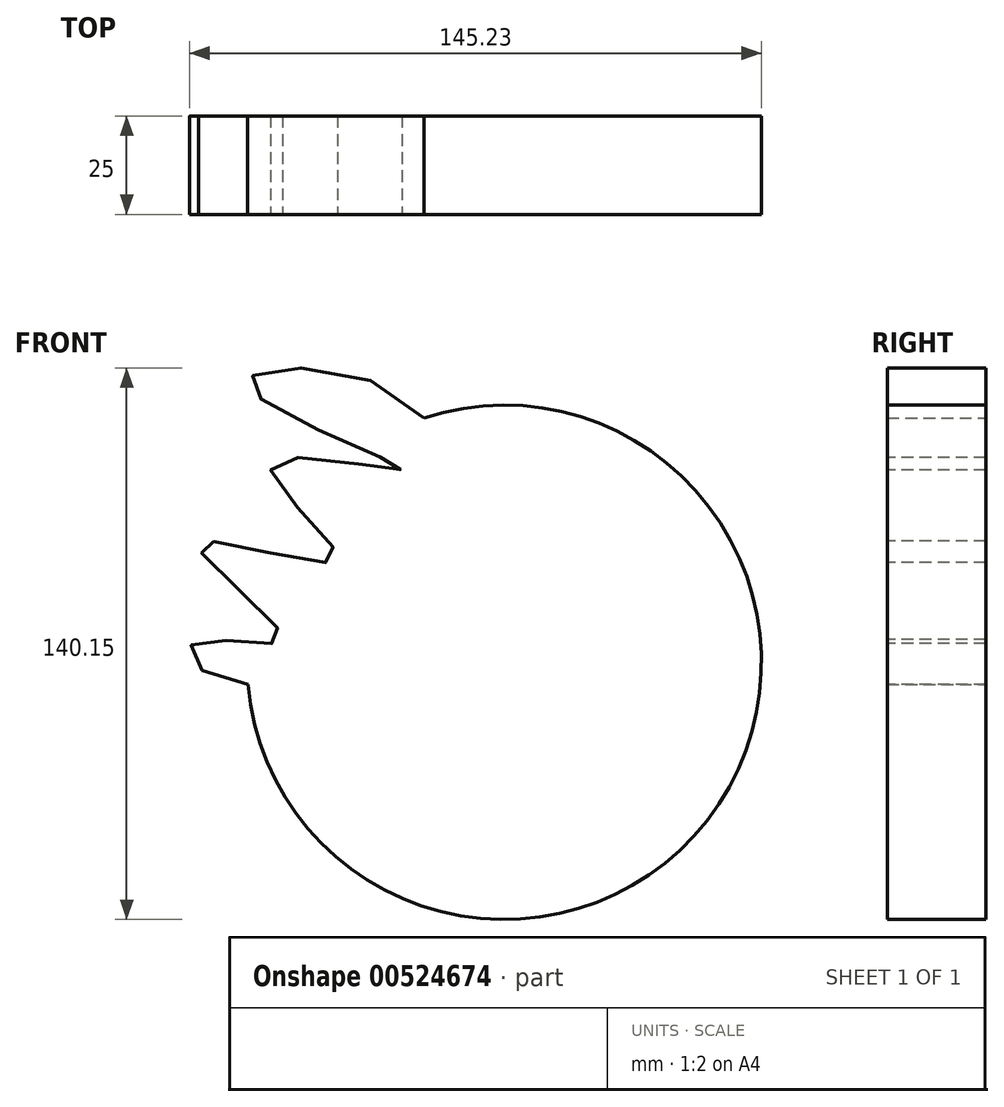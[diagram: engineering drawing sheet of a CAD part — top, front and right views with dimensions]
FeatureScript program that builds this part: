
annotation { "Feature Type Name" : "Feature", "Feature Type Description" : "" }
export const myFeature = defineFeature(function(context is Context, id is Id, definition is map)
    precondition{}
    {
        {
            var Q0;
            Q0=qCreatedBy(makeId("Front.planeOp"),FACE);
            var sketch = newSketch(context, id + "F0", { "sketchPlane" : qUnion([Q0])});
            skArc(sketch, "E0", {"start": v(-74.78, 0) * mm, "mid": v(44.84, -30.44) * mm, "end": v(-30.03, 67.7) * mm});
            skFitSpline(sketch, "E1", {"points": [v(-74.78, 0) * mm, v(-88.66, 10.48) * mm, v(-66, 11.61) * mm, v(-87.25, 35.7) * mm, v(-52.12, 31.73) * mm, v(-68.84, 55.8) * mm, v(-35.7, 54.67) * mm, v(-74.78, 76.2) * mm, v(-30.03, 67.7) * mm, v(-74.78, 0) * mm]});
            skSolve(sketch);
        }
        {
            var Q0;
            {var subQ0=sQuery(id+"F0.wireOp",EDGE,"E0");Q0=makeQuery(id+"F0.imprint","IMPRINT",FACE,{"disambiguationData":[TD([[makeQuery(id+"F0.imprint","IMPRINT",EDGE,{"derivedFrom":subQ0}),1.0]])]});}
            var Q1;
            {var subQ0=sQuery(id+"F0.wireOp",EDGE,"E1");var subQ1=sQuery(id+"F0.wireOp",EDGE,"E0");var subQ2=makeQuery(id+"F0.imprint","INTERSECT",VERTEX,{"disambiguationData":[OD(0.0)],"derivedFrom":[subQ1,subQ0]});Q1=makeQuery(id+"F0.imprint","IMPRINT",FACE,{"disambiguationData":[TD([[makeQuery(id+"F0.imprint","IMPRINT",EDGE,{"disambiguationData":[TD([[subQ2,-1.0]])],"derivedFrom":subQ0}),-1.0]])]});}
            extrude(context, id + "F1", {"entities" : qUnion([Q0, Q1]), "depth" : 25 * mm, "offsetDistance" : 25 * mm});
        }
    });
